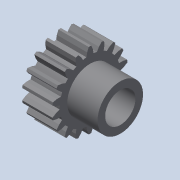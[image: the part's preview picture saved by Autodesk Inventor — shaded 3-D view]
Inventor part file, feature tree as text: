
AUTODESK INVENTOR PART (.ipt)
format: ipt  version: 2020.4 (Build 244396000, 396)  size: 234,496 bytes
history: native  units: mm
features: hole x1, imported_body x1, sketch x1
ambient origin geometry x8: Origin, YZ Plane, XZ Plane, XY Plane, X Axis, Y Axis, Z Axis, Center Point
bodies: Body1 (feature_tree)
feature tree (3):
  hole  "Bohrung1"  [1 undecoded]
  imported_body  "Basis1"
  sketch  "Skizze1"  dims[d0=4.0mm d1=6.0mm d2=4.0mm d3=2.0mm d4=90.0deg d5=8.0mm d6=20.594885mm]
note: 1 required parameter value undecoded (feature->parameter linkage not recoverable at this tier; creation-order binding heuristic only, values carry confidence <= 0.55)
